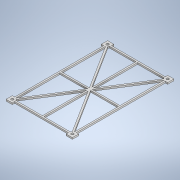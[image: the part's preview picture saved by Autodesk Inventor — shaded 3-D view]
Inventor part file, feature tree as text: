
AUTODESK INVENTOR PART (.ipt)
format: ipt  version: 2020 (Build 240168000, 168)  size: 225,280 bytes
history: native  units: in
note: dims shown in document units (in); Inventor stores cm internally (conversion verified against a paired STEP export)
features: extrude x1, sketch x1
ambient origin geometry x8: Origin, YZ Plane, XZ Plane, XY Plane, X Axis, Y Axis, Z Axis, Center Point
bodies: Solid1 (feature_tree)
feature tree (2):
  extrude  "Extrusion1"  Depth=5.1181in
  sketch  "Sketch1"  dims[d0=3.3465in d1=5.1181in d2=0.315in d3=0.126in d4=0.0787in d5=0.0787in d6=0.0787in d7=0.0787in d8=0.0787in d9=0.0787in d10=0.0787in d11=0.0in d12=0.0394in d13=0.0394in d14=0.0394in d15=0.0394in d16=0.0787in d17=0.0787in]
